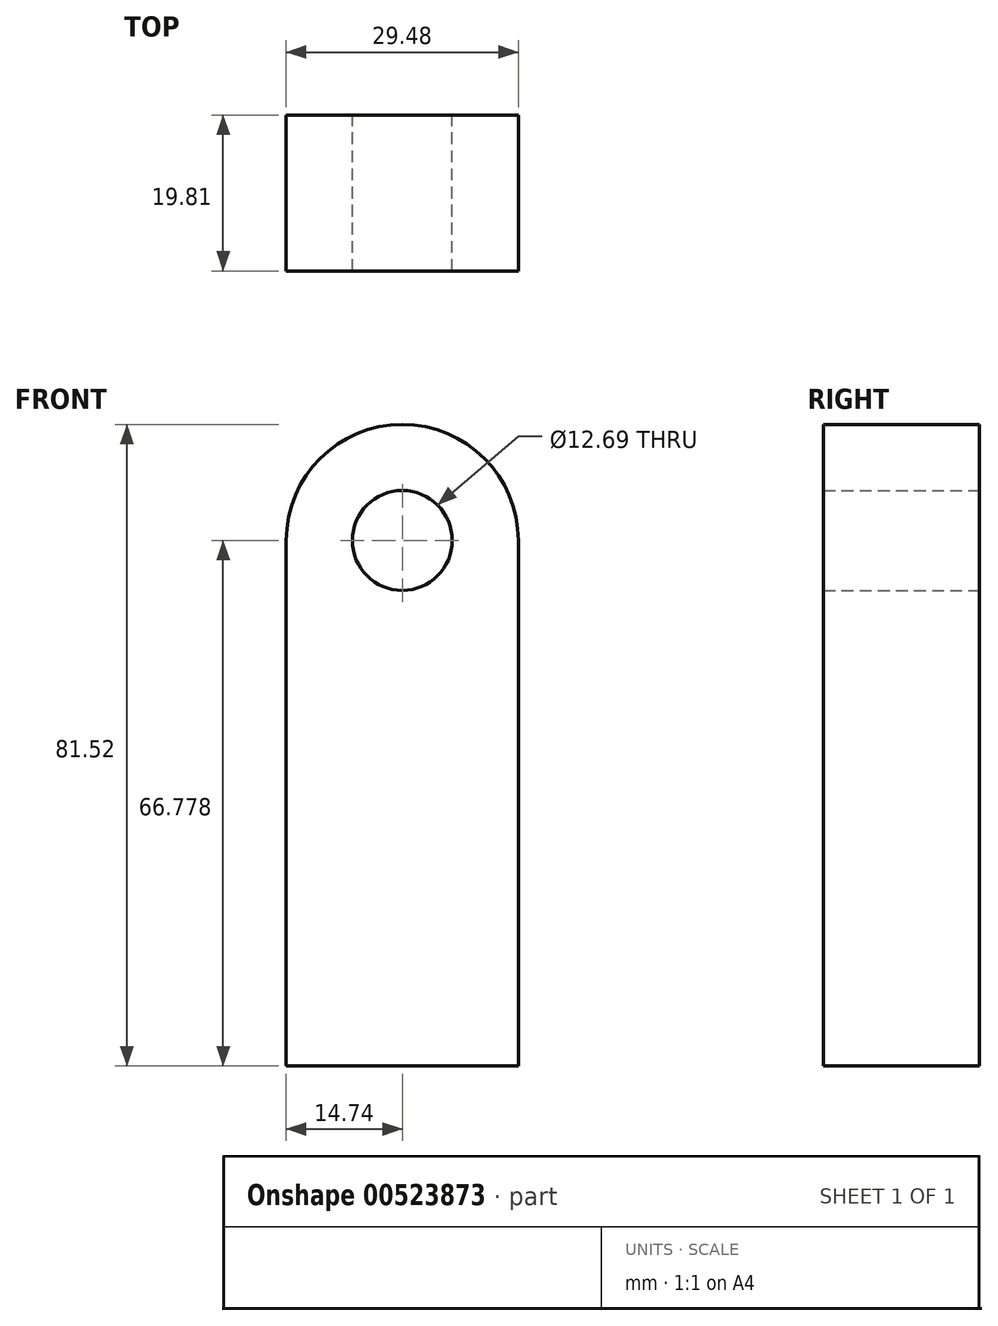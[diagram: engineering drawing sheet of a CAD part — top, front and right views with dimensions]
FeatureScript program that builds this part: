
annotation { "Feature Type Name" : "Feature", "Feature Type Description" : "" }
export const myFeature = defineFeature(function(context is Context, id is Id, definition is map)
    precondition{}
    {
        {
            var Q0;
            Q0=qCreatedBy(makeId("Front.planeOp"),FACE);
            var sketch = newSketch(context, id + "F0", { "sketchPlane" : qUnion([Q0])});
            skLineSegment(sketch, "E0.bottom", {"start": v(14.74, -33.39) * mm, "end": v(-14.74, -33.39) * mm});
            skLineSegment(sketch, "E0.top", {"start": v(14.74, 33.39) * mm, "end": v(-14.74, 33.39) * mm});
            skLineSegment(sketch, "E0.left", {"start": v(14.74, -33.39) * mm, "end": v(14.74, 33.39) * mm});
            skLineSegment(sketch, "E0.right", {"start": v(-14.74, -33.39) * mm, "end": v(-14.74, 33.39) * mm});
            skPoint(sketch, "E0.middle", {"position": v(0, 0) * mm});
            skCircle(sketch, "E1", {"center": v(0, 33.39) * mm, "radius": 14.74 * mm});
            skCircle(sketch, "E2", {"center": v(0, 33.39) * mm, "radius": 6.34 * mm});
            skArc(sketch, "E3", {"start": v(-14.74, 33.39) * mm, "mid": v(0, 48.13) * mm, "end": v(14.74, 33.39) * mm});
            skSolve(sketch);
        }
        {
            var Q0;
            {var subQ1=sQuery(id+"F0.wireOp",EDGE,"E0.top");var subQ3=sQuery(id+"F0.wireOp",EDGE,"E2");var subQ4=makeQuery(id+"F0.imprint","INTERSECT",VERTEX,{"disambiguationData":[OD(0.0)],"derivedFrom":[subQ1,subQ3]});Q0=makeQuery(id+"F0.imprint","IMPRINT",FACE,{"disambiguationData":[TD([[makeQuery(id+"F0.imprint","IMPRINT",EDGE,{"disambiguationData":[TD([[subQ4,-1.0]])],"derivedFrom":subQ3}),-1.0]])]});}
            var Q1;
            {var subQ1=sQuery(id+"F0.wireOp",EDGE,"E0.top");var subQ3=sQuery(id+"F0.wireOp",EDGE,"E2");var subQ4=makeQuery(id+"F0.imprint","INTERSECT",VERTEX,{"disambiguationData":[OD(0.0)],"derivedFrom":[subQ1,subQ3]});Q1=makeQuery(id+"F0.imprint","IMPRINT",FACE,{"disambiguationData":[TD([[makeQuery(id+"F0.imprint","IMPRINT",EDGE,{"disambiguationData":[TD([[subQ4,1.0]])],"derivedFrom":subQ3}),-1.0]])]});}
            var Q2;
            Q2=makeQuery(id+"F0.imprint","IMPRINT",FACE,{"disambiguationData":[TD([[makeQuery(id+"F0.imprint","IMPRINT",EDGE,{"derivedFrom":sQuery(id+"F0.wireOp",EDGE,"E0.bottom")}),-1.0]])]});
            extrude(context, id + "F1", {"entities" : qUnion([Q0, Q1, Q2]), "depth" : 19.8 * mm, "offsetDistance" : 25.4 * mm});
        }
    });
